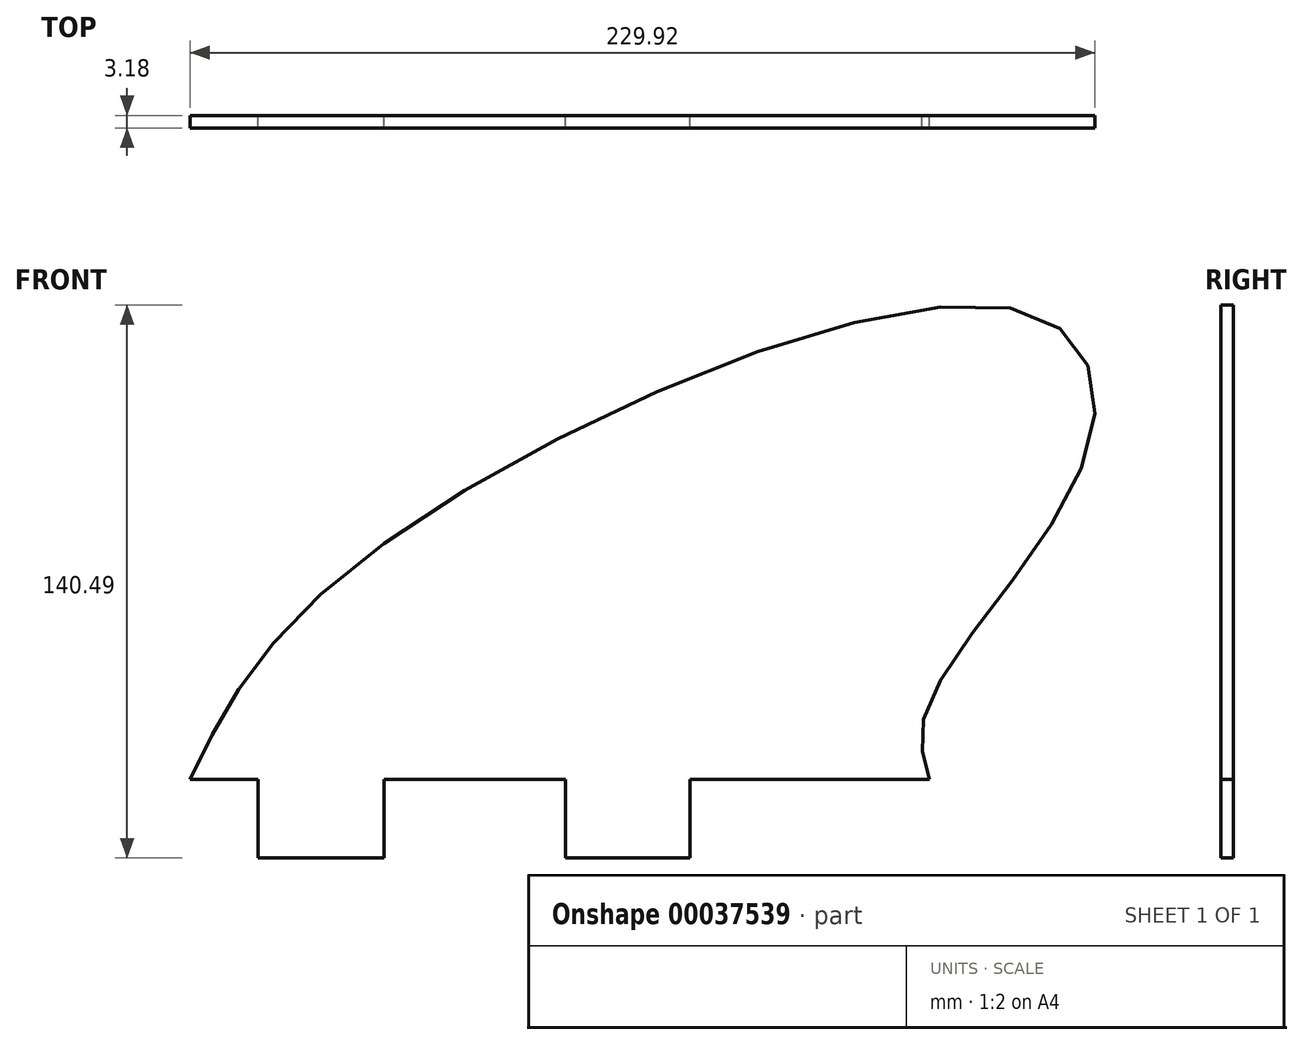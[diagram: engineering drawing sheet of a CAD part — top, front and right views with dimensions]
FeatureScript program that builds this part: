
annotation { "Feature Type Name" : "Feature", "Feature Type Description" : "" }
export const myFeature = defineFeature(function(context is Context, id is Id, definition is map)
    precondition{}
    {
        {
            var Q0;
            Q0=qCreatedBy(makeId("Front.planeOp"),FACE);
            var sketch = newSketch(context, id + "F0", { "sketchPlane" : qUnion([Q0])});
            skLineSegment(sketch, "E0", {"start": v(-75.3, -56.37) * mm, "end": v(-58, -56.37) * mm});
            skLineSegment(sketch, "E1", {"start": v(-58, -56.37) * mm, "end": v(-58, -76.31) * mm});
            skLineSegment(sketch, "E2", {"start": v(-58, -76.31) * mm, "end": v(-26.05, -76.31) * mm});
            skLineSegment(sketch, "E3", {"start": v(-26.05, -76.31) * mm, "end": v(-26.05, -56.37) * mm});
            skLineSegment(sketch, "E4", {"start": v(-26.05, -56.37) * mm, "end": v(20.15, -56.37) * mm});
            skLineSegment(sketch, "E5", {"start": v(20.15, -56.37) * mm, "end": v(20.15, -76.31) * mm});
            skLineSegment(sketch, "E6", {"start": v(20.15, -76.31) * mm, "end": v(51.69, -76.31) * mm});
            skLineSegment(sketch, "E7", {"start": v(51.69, -76.31) * mm, "end": v(51.69, -56.37) * mm});
            skLineSegment(sketch, "E8", {"start": v(51.69, -56.37) * mm, "end": v(112.53, -56.37) * mm});
            skFitSpline(sketch, "E9", {"points": [v(-75.3, -56.37) * mm, v(-30.93, 0) * mm, v(135.73, 62.88) * mm, v(152.83, 27.47) * mm, v(112.53, -36.63) * mm, v(112.53, -56.37) * mm], "startDerivative": vector(126.5, 261) * mm, "endDerivative": vector(48.05, -160.6) * mm});
            skSolve(sketch);
        }
        {
            var Q0;
            Q0=makeQuery(id+"F0.imprint","IMPRINT",FACE,{"disambiguationData":[TD([[makeQuery(id+"F0.imprint","IMPRINT",EDGE,{"derivedFrom":sQuery(id+"F0.wireOp",EDGE,"E0")}),1.0]])]});
            extrude(context, id + "F1", {"entities" : qUnion([Q0]), "depth" : 3.18 * mm});
        }
    });
